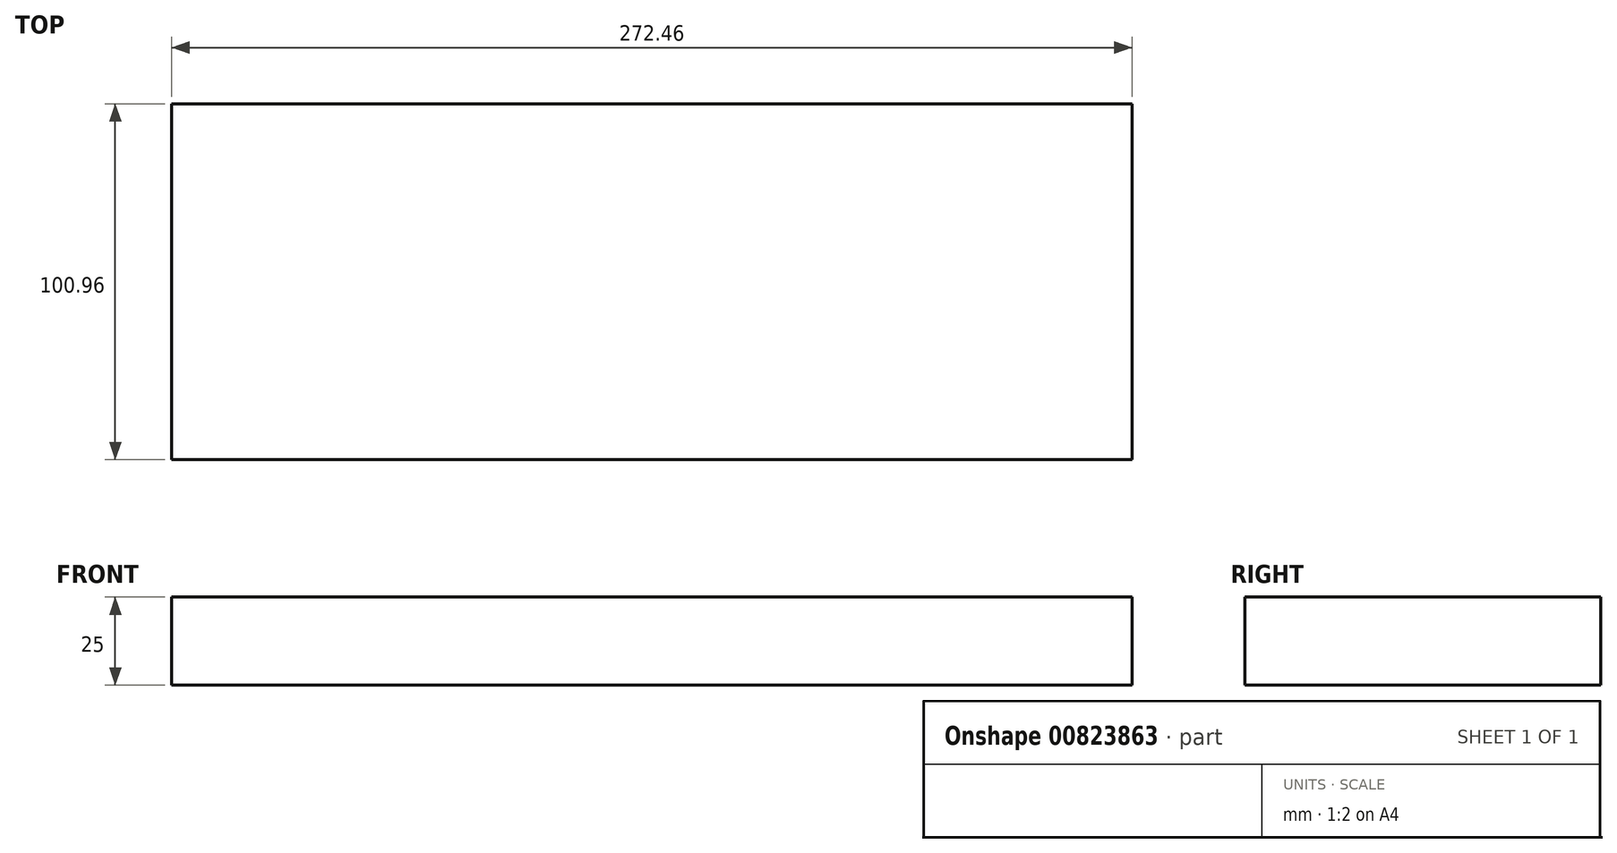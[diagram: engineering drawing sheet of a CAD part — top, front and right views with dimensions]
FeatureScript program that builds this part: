
annotation { "Feature Type Name" : "Feature", "Feature Type Description" : "" }
export const myFeature = defineFeature(function(context is Context, id is Id, definition is map)
    precondition{}
    {
        {
            var Q0;
            Q0=qCreatedBy(makeId("Top.planeOp"),FACE);
            var sketch = newSketch(context, id + "F0", { "sketchPlane" : qUnion([Q0])});
            skLineSegment(sketch, "E0.bottom", {"start": v(-136.23, 50.48) * mm, "end": v(136.23, 50.48) * mm});
            skLineSegment(sketch, "E0.top", {"start": v(-136.23, -50.48) * mm, "end": v(136.23, -50.48) * mm});
            skLineSegment(sketch, "E0.left", {"start": v(-136.23, 50.48) * mm, "end": v(-136.23, -50.48) * mm});
            skLineSegment(sketch, "E0.right", {"start": v(136.23, 50.48) * mm, "end": v(136.23, -50.48) * mm});
            skPoint(sketch, "E0.middle", {"position": v(0, 0) * mm});
            skSolve(sketch);
        }
        {
            var Q0;
            Q0=makeQuery(id+"F0.imprint","IMPRINT",FACE,{"disambiguationData":[TD([[makeQuery(id+"F0.imprint","IMPRINT",EDGE,{"derivedFrom":sQuery(id+"F0.wireOp",EDGE,"E0.bottom")}),-1.0]])]});
            extrude(context, id + "F1", {"entities" : qUnion([Q0]), "depth" : 25 * mm, "offsetDistance" : 25 * mm});
        }
    });
